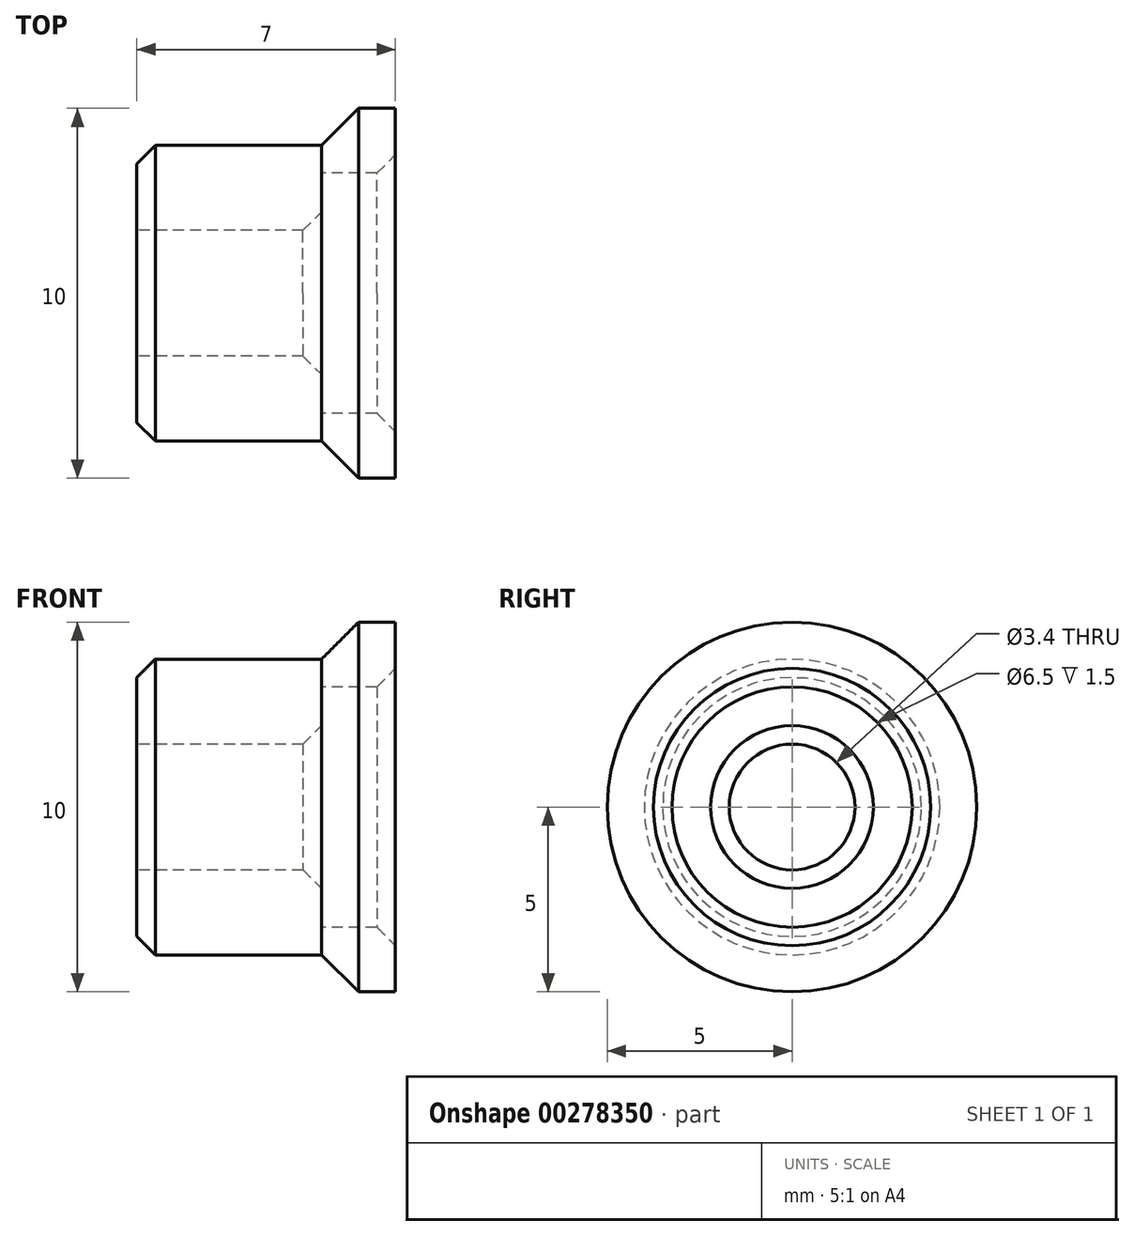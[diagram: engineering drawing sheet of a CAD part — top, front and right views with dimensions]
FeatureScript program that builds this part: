
annotation { "Feature Type Name" : "Feature", "Feature Type Description" : "" }
export const myFeature = defineFeature(function(context is Context, id is Id, definition is map)
    precondition{}
    {
        {
            var Q0;
            Q0=qCreatedBy(makeId("Front.planeOp"),FACE);
            var sketch = newSketch(context, id + "F0", { "sketchPlane" : qUnion([Q0])});
            skLineSegment(sketch, "E0", {"start": v(0, 0) * mm, "end": v(0, 2.3) * mm});
            skLineSegment(sketch, "E1", {"start": v(0, 2.3) * mm, "end": v(5, 2.3) * mm});
            skLineSegment(sketch, "E2", {"start": v(5, 2.3) * mm, "end": v(6, 3.3) * mm});
            skLineSegment(sketch, "E3", {"start": v(6, 3.3) * mm, "end": v(7, 3.3) * mm});
            skLineSegment(sketch, "E4", {"start": v(7, 3.3) * mm, "end": v(7, 1.55) * mm});
            skLineSegment(sketch, "E5", {"start": v(5, 0) * mm, "end": v(0, 0) * mm});
            skLineSegment(sketch, "E6", {"start": v(0, 0) * mm, "end": v(0, -1.7) * mm, "construction": true});
            skLineSegment(sketch, "E7", {"start": v(0, -1.7) * mm, "end": v(7, -1.7) * mm});
            skLineSegment(sketch, "E8", {"start": v(7, -1.7) * mm, "end": v(7, 1.55) * mm, "construction": true});
            skLineSegment(sketch, "E9", {"start": v(7, 1.55) * mm, "end": v(5, 1.55) * mm});
            skLineSegment(sketch, "E10", {"start": v(5, 1.55) * mm, "end": v(5, 0) * mm});
            skSolve(sketch);
        }
        {
            var Q0;
            Q0=makeQuery(id+"F0.imprint","IMPRINT",FACE,{"disambiguationData":[TD([[makeQuery(id+"F0.imprint","IMPRINT",EDGE,{"derivedFrom":sQuery(id+"F0.wireOp",EDGE,"E0")}),-1.0]])]});
            var Q1;
            Q1=sQuery(id+"F0.wireOp",EDGE,"E7");
            revolve(context, id + "F1", {"entities" : qUnion([Q0]), "axis" : qUnion([Q1]), "revolveType" : RevolveType.FULL});
        }
        {
            var Q0;
            Q0=makeQuery(id+"F1.opRevolve","SWEPT_EDGE",EDGE,{"disambiguationData":[OSD([sQuery(id+"F0.wireOp",EDGE,"E5"),sQuery(id+"F0.wireOp",EDGE,"E10")])]});
            var Q1;
            Q1=makeQuery(id+"F1.opRevolve","SWEPT_EDGE",EDGE,{"disambiguationData":[OSD([sQuery(id+"F0.wireOp",EDGE,"E4"),sQuery(id+"F0.wireOp",EDGE,"E9")])]});
            chamfer(context, id + "F2", {"entities" : qUnion([Q0, Q1]), "width" : 0.5 * mm, "tangentPropagation" : true});
        }
        {
            var Q0;
            Q0=makeQuery(id+"F1.opRevolve","SWEPT_EDGE",EDGE,{"disambiguationData":[OSD([sQuery(id+"F0.wireOp",EDGE,"E0"),sQuery(id+"F0.wireOp",EDGE,"E1")])]});
            chamfer(context, id + "F3", {"entities" : qUnion([Q0]), "width" : 0.5 * mm, "tangentPropagation" : true});
        }
    });
